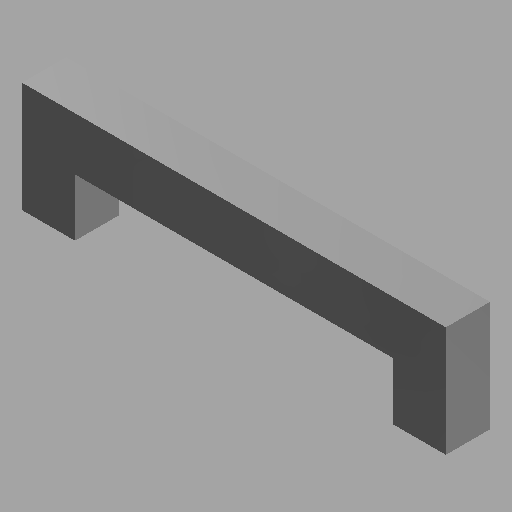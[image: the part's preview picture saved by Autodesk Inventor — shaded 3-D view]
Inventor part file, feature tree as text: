
AUTODESK INVENTOR PART (.ipt)
format: ipt  version: 2023 (Build 270158030, 158C)  size: 94,720 bytes
history: native  units: mm (DEFAULTED — no unit token found)
features: other x1, extrude x1, sketch x1
ambient origin geometry x8: Origin, YZ Plane, XZ Plane, XY Plane, X Axis, Y Axis, Z Axis, Center Point
bodies: Solid1 (feature_tree)
feature tree (3):
  other  "Block header 2"
  extrude  "Extrusion1"  Depth=165.1mm
  sketch  "Sketch1"  dims[d0=914.4mm d1=165.1mm d2=25.4mm d3=0.0mm]
